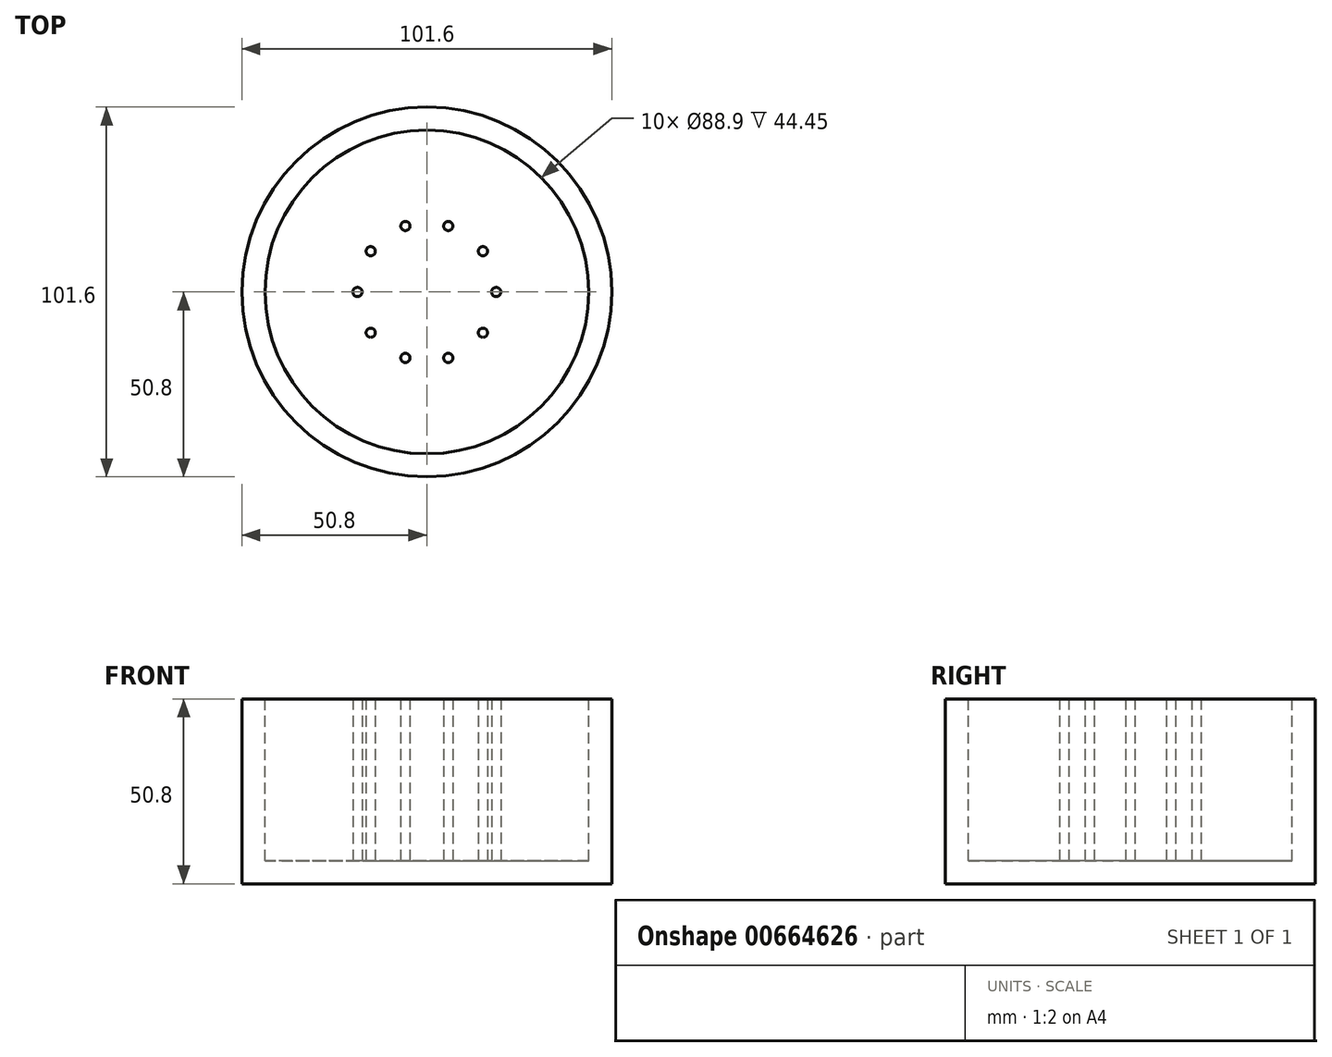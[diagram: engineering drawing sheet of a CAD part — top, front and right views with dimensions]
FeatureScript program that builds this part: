
annotation { "Feature Type Name" : "Feature", "Feature Type Description" : "" }
export const myFeature = defineFeature(function(context is Context, id is Id, definition is map)
    precondition{}
    {
        {
            var Q0;
            Q0=qCreatedBy(makeId("Top.planeOp"),FACE);
            var sketch = newSketch(context, id + "F0", { "sketchPlane" : qUnion([Q0])});
            skCircle(sketch, "E0", {"center": v(0, 0) * mm, "radius": 50.8 * mm});
            skSolve(sketch);
        }
        {
            var Q0;
            Q0=makeQuery(id+"F0.imprint","IMPRINT",FACE,{"disambiguationData":[TD([[makeQuery(id+"F0.imprint","IMPRINT",EDGE,{"derivedFrom":sQuery(id+"F0.wireOp",EDGE,"E0")}),1.0]])]});
            extrude(context, id + "F1", {"entities" : qUnion([Q0]), "depth" : 50.8 * mm, "offsetDistance" : 25.4 * mm});
        }
        {
            var Q0;
            Q0=makeQuery(id+"F1.opExtrude","CAP_FACE",FACE,{"disambiguationData":[OSD([sQuery(id+"F0.wireOp",EDGE,"E0")])],"isStart":false});
            var sketch = newSketch(context, id + "F2", { "sketchPlane" : qUnion([Q0])});
            skCircle(sketch, "E1", {"center": v(0, 0) * mm, "radius": 44.45 * mm});
            skSolve(sketch);
        }
        {
            var Q0;
            Q0=makeQuery(id+"F2.imprint","IMPRINT",FACE,{"disambiguationData":[TD([[makeQuery(id+"F2.imprint","IMPRINT",EDGE,{"derivedFrom":sQuery(id+"F2.wireOp",EDGE,"E1")}),1.0]])]});
            extrude(context, id + "F3", {"entities" : qUnion([Q0]), "operationType" : NewBodyOperationType.REMOVE, "oppositeDirection" : true, "depth" : 44.45 * mm, "offsetDistance" : 25.4 * mm});
        }
        {
            var Q0;
            Q0=makeQuery(id+"F3.boolean.opBoolean","COPY",FACE,{"derivedFrom":makeQuery(id+"F3.opExtrude","CAP_FACE",FACE,{"disambiguationData":[OSD([sQuery(id+"F2.wireOp",EDGE,"E1")])],"isStart":false})});
            var sketch = newSketch(context, id + "F4", { "sketchPlane" : qUnion([Q0])});
            skCircle(sketch, "E2", {"center": v(0, 0) * mm, "radius": 19.05 * mm});
            skSolve(sketch);
        }
        {
            var Q0;
            Q0=makeQuery(id+"F4.imprint","IMPRINT",FACE,{"disambiguationData":[TD([[makeQuery(id+"F4.imprint","IMPRINT",EDGE,{"derivedFrom":sQuery(id+"F4.wireOp",EDGE,"E2")}),-1.0]])]});
            var sketch = newSketch(context, id + "F5", { "sketchPlane" : qUnion([Q0])});
            skCircle(sketch, "E3", {"center": v(-19.05, 0) * mm, "radius": 1.27 * mm});
            skSolve(sketch);
        }
        {
            var Q0;
            Q0 = qSketchRegion(id + "F5", true);
            extrude(context, id + "F6", {"entities" : qUnion([Q0]), "operationType" : NewBodyOperationType.ADD, "depth" : 44.45 * mm, "offsetDistance" : 25.4 * mm});
        }
        {
            var Q0;
            Q0=qCreatedBy(makeId("Right.planeOp"),FACE);
            var sketch = newSketch(context, id + "F7", { "sketchPlane" : qUnion([Q0])});
            skLineSegment(sketch, "E4", {"start": v(0, 7.45) * mm, "end": v(0, 51.83) * mm});
            skSolve(sketch);
        }
        {
            var Q0;
            Q0=makeQuery(id+"F1.opExtrude","SWEPT_BODY",BODY,{"disambiguationData":[OSD([sQuery(id+"F0.wireOp",EDGE,"E0")])]});
            var Q1;
            Q1=sQuery(id+"F7.wireOp",EDGE,"E4");
            circularPattern(context, id + "F8", {"entities" : qUnion([Q0]), "axis" : qUnion([Q1]), "angle" : 360 * degree, "instanceCount" : 10, "oppositeDirection" : true, "equalSpace" : true});
        }
    });
